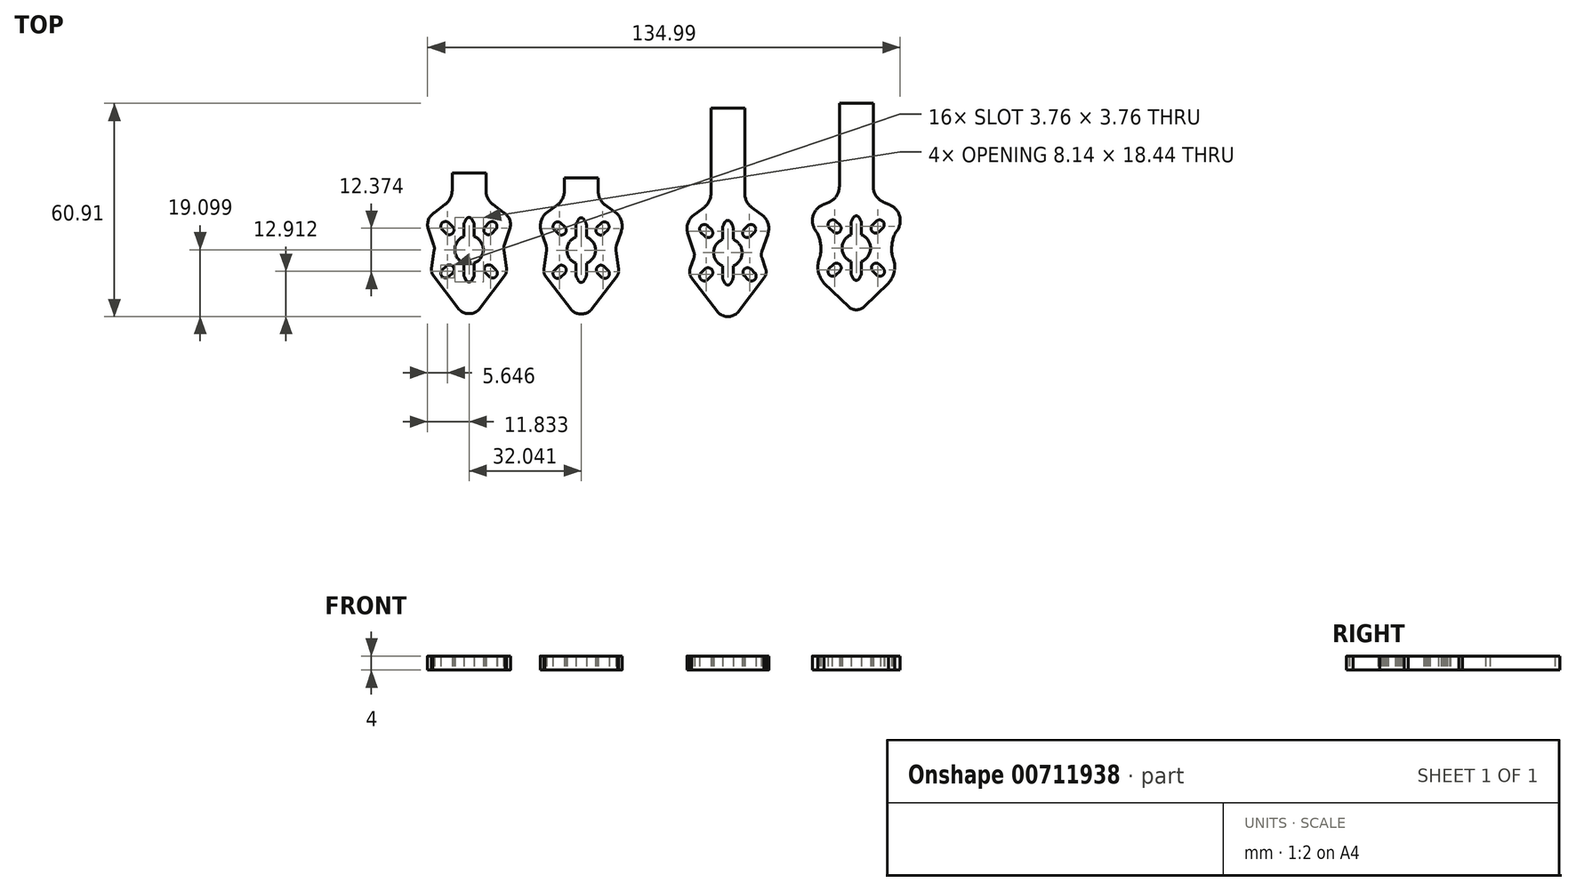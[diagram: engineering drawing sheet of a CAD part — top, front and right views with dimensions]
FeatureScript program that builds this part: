
annotation { "Feature Type Name" : "Feature", "Feature Type Description" : "" }
export const myFeature = defineFeature(function(context is Context, id is Id, definition is map)
    precondition{}
    {
        {
            var Q0;
            Q0=qCreatedBy(makeId("Top.planeOp"),FACE);
            var sketch = newSketch(context, id + "F0", { "sketchPlane" : qUnion([Q0])});
            skLineSegment(sketch, "E0", {"start": v(60.05, 27.48) * mm, "end": v(60.05, 10.08) * mm, "construction": true});
            skLineSegment(sketch, "E1", {"start": v(60.05, 27.48) * mm, "end": v(45.07, 12.5) * mm, "construction": true});
            skArc(sketch, "E2", {"start": v(53.44, 32.18) * mm, "mid": v(55.35, 32.18) * mm, "end": v(55.35, 34.1) * mm});
            skArc(sketch, "E3", {"start": v(54.29, 35.15) * mm, "mid": v(52.38, 35.15) * mm, "end": v(52.38, 33.24) * mm});
            skLineSegment(sketch, "E4", {"start": v(55.35, 34.1) * mm, "end": v(54.29, 35.15) * mm});
            skLineSegment(sketch, "E5.MirrorCS", {"start": v(53.44, 32.18) * mm, "end": v(52.38, 33.24) * mm});
            skLineSegment(sketch, "E6.MirrorCS", {"start": v(66.56, 32.18) * mm, "end": v(67.62, 33.24) * mm});
            skArc(sketch, "E7.MirrorCS", {"start": v(65.71, 35.15) * mm, "mid": v(67.62, 35.15) * mm, "end": v(67.62, 33.24) * mm});
            skLineSegment(sketch, "E8.MirrorCS", {"start": v(64.65, 34.1) * mm, "end": v(65.71, 35.15) * mm});
            skArc(sketch, "E9.MirrorCS", {"start": v(66.56, 32.18) * mm, "mid": v(64.65, 32.18) * mm, "end": v(64.65, 34.1) * mm});
            skLineSegment(sketch, "E10.MirrorCS", {"start": v(64.75, 20.87) * mm, "end": v(65.81, 19.8) * mm});
            skLineSegment(sketch, "E11.MirrorCS", {"start": v(66.66, 22.78) * mm, "end": v(67.72, 21.72) * mm});
            skArc(sketch, "E12.MirrorCS", {"start": v(66.66, 22.78) * mm, "mid": v(64.75, 22.78) * mm, "end": v(64.75, 20.87) * mm});
            skArc(sketch, "E13.MirrorCS", {"start": v(65.81, 19.8) * mm, "mid": v(67.72, 19.8) * mm, "end": v(67.72, 21.72) * mm});
            skLineSegment(sketch, "E14.MirrorCS", {"start": v(55.35, 20.87) * mm, "end": v(54.29, 19.8) * mm});
            skLineSegment(sketch, "E15.MirrorCS", {"start": v(53.44, 22.78) * mm, "end": v(52.38, 21.72) * mm});
            skArc(sketch, "E16.MirrorCS", {"start": v(54.29, 19.8) * mm, "mid": v(52.38, 19.8) * mm, "end": v(52.38, 21.72) * mm});
            skArc(sketch, "E17.MirrorCS", {"start": v(53.44, 22.78) * mm, "mid": v(55.35, 22.78) * mm, "end": v(55.35, 20.87) * mm});
            skLineSegment(sketch, "E18.left", {"start": v(61.55, 20.5) * mm, "end": v(61.55, 23.7) * mm});
            skLineSegment(sketch, "E18.right", {"start": v(58.55, 20.5) * mm, "end": v(58.55, 23.7) * mm});
            skLineSegment(sketch, "E19.trimOffspring", {"start": v(58.55, 31.27) * mm, "end": v(58.55, 34.46) * mm});
            skLineSegment(sketch, "E20.trimOffspring", {"start": v(61.55, 31.27) * mm, "end": v(61.55, 34.46) * mm});
            skArc(sketch, "E21.MirrorCS", {"start": v(69.32, 26.9) * mm, "mid": v(69.38, 26.86) * mm, "end": v(69.43, 26.82) * mm});
            skArc(sketch, "E22.MirrorCS", {"start": v(58.8, 35.43) * mm, "mid": v(58.61, 34.96) * mm, "end": v(58.55, 34.46) * mm});
            skArc(sketch, "E23.MirrorCS", {"start": v(61.55, 34.46) * mm, "mid": v(61.48, 34.96) * mm, "end": v(61.3, 35.43) * mm});
            skArc(sketch, "E24.MirrorCS", {"start": v(61.55, 20.5) * mm, "mid": v(61.48, 20) * mm, "end": v(61.3, 19.53) * mm});
            skArc(sketch, "E25.MirrorCS", {"start": v(58.8, 19.53) * mm, "mid": v(58.61, 20) * mm, "end": v(58.55, 20.5) * mm});
            skCircle(sketch, "E26", {"center": v(60.05, 27.48) * mm, "radius": 8 * mm, "construction": true});
            skLineSegment(sketch, "E27.MirrorCS", {"start": v(61.3, 35.43) * mm, "end": v(60.86, 36.22) * mm});
            skLineSegment(sketch, "E28.MirrorCS", {"start": v(58.8, 35.43) * mm, "end": v(59.24, 36.22) * mm});
            skArc(sketch, "E29.MirrorCS", {"start": v(59.24, 36.22) * mm, "mid": v(60.05, 36.7) * mm, "end": v(60.86, 36.22) * mm});
            skLineSegment(sketch, "E30.MirrorCS", {"start": v(61.95, 38.08) * mm, "end": v(58.14, 38.08) * mm});
            skPoint(sketch, "E31.visualSharp", {"position": v(68.55, 34.93) * mm});
            skPoint(sketch, "E32.MirrorCS.start.orphan", {"position": v(51.55, 36.03) * mm});
            skPoint(sketch, "E33.visualSharp", {"position": v(65.05, 10.08) * mm});
            skPoint(sketch, "E34.orphan", {"position": v(63.42, 8.64) * mm});
            skPoint(sketch, "E35", {"position": v(60.05, 38.9) * mm});
            skLineSegment(sketch, "E36.bottom", {"start": v(55.05, 68.82) * mm, "end": v(65.05, 68.82) * mm});
            skLineSegment(sketch, "E36.right", {"start": v(64.88, 70.85) * mm, "end": v(64.88, 45.12) * mm});
            skPoint(sketch, "E36.middle", {"position": v(60.05, 53.86) * mm});
            skPoint(sketch, "E37", {"position": v(60.05, 36.7) * mm});
            skPoint(sketch, "E38", {"position": v(60.05, 36.98) * mm});
            skArc(sketch, "E39", {"start": v(61.55, 23.7) * mm, "mid": v(64.12, 27.48) * mm, "end": v(61.55, 31.27) * mm});
            skArc(sketch, "E40.trimOffspring", {"start": v(58.55, 31.27) * mm, "mid": v(55.98, 27.48) * mm, "end": v(58.55, 23.7) * mm});
            skPoint(sketch, "E41.MirrorP", {"position": v(55.21, 43.47) * mm});
            skLineSegment(sketch, "E42.MirrorCS", {"start": v(55.21, 70.85) * mm, "end": v(55.21, 45.12) * mm});
            skArc(sketch, "E43.MirrorCS", {"start": v(55.21, 45.12) * mm, "mid": v(54.67, 42.86) * mm, "end": v(53.17, 41.08) * mm});
            skPoint(sketch, "E44.MirrorCS.end.orphan", {"position": v(50.72, 39.97) * mm});
            skPoint(sketch, "E45.orphan", {"position": v(68.4, 16.34) * mm});
            skPoint(sketch, "E46.orphan", {"position": v(51.7, 16.34) * mm});
            skPoint(sketch, "E47.visualSharp", {"position": v(60.05, 7.98) * mm});
            skPoint(sketch, "E48", {"position": v(48.43, 32.67) * mm});
            skArc(sketch, "E49", {"start": v(49.82, 25.54) * mm, "mid": v(49.84, 28.62) * mm, "end": v(49, 31.57) * mm});
            skArc(sketch, "E50", {"start": v(49.42, 24.36) * mm, "mid": v(49.65, 24.94) * mm, "end": v(49.82, 25.54) * mm});
            skPoint(sketch, "E51.start.orphan", {"position": v(50.18, 17.36) * mm});
            skArc(sketch, "E52", {"start": v(49.42, 24.36) * mm, "mid": v(49.23, 20.72) * mm, "end": v(50.84, 17.45) * mm});
            skArc(sketch, "E53.MirrorCS", {"start": v(70.68, 24.36) * mm, "mid": v(70.87, 20.72) * mm, "end": v(69.26, 17.45) * mm});
            skArc(sketch, "E54", {"start": v(50.72, 39.97) * mm, "mid": v(47.68, 36.65) * mm, "end": v(48.59, 32.24) * mm});
            skArc(sketch, "E55", {"start": v(50.72, 39.97) * mm, "mid": v(51.97, 40.47) * mm, "end": v(53.17, 41.08) * mm});
            skArc(sketch, "E56.filletArc", {"start": v(49, 31.57) * mm, "mid": v(48.81, 31.92) * mm, "end": v(48.59, 32.24) * mm});
            skArc(sketch, "E57.MirrorCS", {"start": v(64.88, 45.12) * mm, "mid": v(65.42, 42.86) * mm, "end": v(66.93, 41.08) * mm});
            skArc(sketch, "E58.MirrorCS", {"start": v(70.28, 25.54) * mm, "mid": v(70.26, 28.62) * mm, "end": v(71.1, 31.57) * mm});
            skArc(sketch, "E59.MirrorCS", {"start": v(70.68, 24.36) * mm, "mid": v(70.45, 24.94) * mm, "end": v(70.28, 25.54) * mm});
            skCircle(sketch, "E60", {"center": v(60.05, 27.48) * mm, "radius": 14.15 * mm, "construction": true});
            skLineSegment(sketch, "E61", {"start": v(50.84, 17.45) * mm, "end": v(57.89, 10.7) * mm});
            skLineSegment(sketch, "E62.MirrorCS", {"start": v(69.26, 17.45) * mm, "end": v(62.2, 10.7) * mm});
            skArc(sketch, "E63", {"start": v(57.89, 10.7) * mm, "mid": v(60.05, 9.84) * mm, "end": v(62.2, 10.7) * mm});
            skPoint(sketch, "E64.start.orphan", {"position": v(57.77, 9.43) * mm});
            skPoint(sketch, "E65.orphan", {"position": v(62.32, 9.43) * mm});
            skPoint(sketch, "E66.MirrorCS.end.orphan", {"position": v(69.26, 18.55) * mm});
            skPoint(sketch, "E67.MirrorCS.start.orphan", {"position": v(70.68, 24.36) * mm});
            skPoint(sketch, "E68.MirrorCS.end.orphan", {"position": v(71.5, 32.24) * mm});
            skPoint(sketch, "E69.orphan", {"position": v(71.1, 31.57) * mm});
            skArc(sketch, "E70.MirrorCS", {"start": v(69.38, 39.97) * mm, "mid": v(72.42, 36.65) * mm, "end": v(71.5, 32.24) * mm});
            skArc(sketch, "E71.MirrorCS", {"start": v(71.1, 31.57) * mm, "mid": v(71.28, 31.92) * mm, "end": v(71.5, 32.24) * mm});
            skPoint(sketch, "E72.orphan", {"position": v(66.93, 41.08) * mm});
            skPoint(sketch, "E73.MirrorCS.start.orphan", {"position": v(69.38, 39.97) * mm});
            skArc(sketch, "E74.MirrorCS", {"start": v(69.38, 39.97) * mm, "mid": v(68.13, 40.47) * mm, "end": v(66.93, 41.08) * mm});
            skLineSegment(sketch, "E75", {"start": v(60.05, 27.48) * mm, "end": v(61.4, 27.48) * mm, "construction": true});
            skLineSegment(sketch, "E76.MirrorCS", {"start": v(61.3, 19.53) * mm, "end": v(60.86, 18.74) * mm});
            skLineSegment(sketch, "E77.MirrorCS", {"start": v(58.8, 19.53) * mm, "end": v(59.24, 18.74) * mm});
            skArc(sketch, "E78.MirrorCS", {"start": v(59.24, 18.74) * mm, "mid": v(60.05, 18.26) * mm, "end": v(60.86, 18.74) * mm});
            skLineSegment(sketch, "E79", {"start": v(23.37, 26.17) * mm, "end": v(23.37, 8.78) * mm, "construction": true});
            skLineSegment(sketch, "E80", {"start": v(23.37, 26.17) * mm, "end": v(8.4, 11.2) * mm, "construction": true});
            skArc(sketch, "E81", {"start": v(16.76, 30.87) * mm, "mid": v(18.67, 30.87) * mm, "end": v(18.67, 32.78) * mm});
            skArc(sketch, "E82", {"start": v(17.6, 33.84) * mm, "mid": v(15.7, 33.84) * mm, "end": v(15.7, 31.93) * mm});
            skLineSegment(sketch, "E83", {"start": v(18.67, 32.78) * mm, "end": v(17.6, 33.84) * mm});
            skLineSegment(sketch, "E84.MirrorCS", {"start": v(16.76, 30.87) * mm, "end": v(15.7, 31.93) * mm});
            skLineSegment(sketch, "E85.MirrorCS", {"start": v(29.88, 30.87) * mm, "end": v(30.94, 31.93) * mm});
            skArc(sketch, "E86.MirrorCS", {"start": v(29.03, 33.84) * mm, "mid": v(30.94, 33.84) * mm, "end": v(30.94, 31.93) * mm});
            skLineSegment(sketch, "E87.MirrorCS", {"start": v(27.97, 32.78) * mm, "end": v(29.03, 33.84) * mm});
            skArc(sketch, "E88.MirrorCS", {"start": v(29.88, 30.87) * mm, "mid": v(27.97, 30.87) * mm, "end": v(27.97, 32.78) * mm});
            skLineSegment(sketch, "E89.MirrorCS", {"start": v(28.07, 19.56) * mm, "end": v(29.13, 18.5) * mm});
            skLineSegment(sketch, "E90.MirrorCS", {"start": v(29.98, 21.47) * mm, "end": v(31.04, 20.4) * mm});
            skArc(sketch, "E91.MirrorCS", {"start": v(29.98, 21.47) * mm, "mid": v(28.07, 21.47) * mm, "end": v(28.07, 19.56) * mm});
            skArc(sketch, "E92.MirrorCS", {"start": v(29.13, 18.5) * mm, "mid": v(31.04, 18.5) * mm, "end": v(31.04, 20.4) * mm});
            skLineSegment(sketch, "E93.MirrorCS", {"start": v(18.67, 19.56) * mm, "end": v(17.6, 18.5) * mm});
            skLineSegment(sketch, "E94.MirrorCS", {"start": v(16.76, 21.47) * mm, "end": v(15.7, 20.4) * mm});
            skArc(sketch, "E95.MirrorCS", {"start": v(17.6, 18.5) * mm, "mid": v(15.7, 18.5) * mm, "end": v(15.7, 20.4) * mm});
            skArc(sketch, "E96.MirrorCS", {"start": v(16.76, 21.47) * mm, "mid": v(18.67, 21.47) * mm, "end": v(18.67, 19.56) * mm});
            skLineSegment(sketch, "E97.left", {"start": v(24.87, 19.19) * mm, "end": v(24.87, 22.38) * mm});
            skLineSegment(sketch, "E97.right", {"start": v(21.87, 19.19) * mm, "end": v(21.87, 22.38) * mm});
            skLineSegment(sketch, "E98.trimOffspring", {"start": v(21.87, 29.96) * mm, "end": v(21.87, 33.15) * mm});
            skLineSegment(sketch, "E99.trimOffspring", {"start": v(24.87, 29.96) * mm, "end": v(24.87, 33.15) * mm});
            skArc(sketch, "E100.MirrorCS", {"start": v(22.12, 34.12) * mm, "mid": v(21.93, 33.65) * mm, "end": v(21.87, 33.15) * mm});
            skArc(sketch, "E101.MirrorCS", {"start": v(24.87, 33.15) * mm, "mid": v(24.8, 33.65) * mm, "end": v(24.62, 34.12) * mm});
            skArc(sketch, "E102.MirrorCS", {"start": v(24.87, 19.19) * mm, "mid": v(24.8, 18.69) * mm, "end": v(24.62, 18.22) * mm});
            skArc(sketch, "E103.MirrorCS", {"start": v(22.12, 18.22) * mm, "mid": v(21.93, 18.69) * mm, "end": v(21.87, 19.19) * mm});
            skCircle(sketch, "E104", {"center": v(23.37, 26.17) * mm, "radius": 8 * mm, "construction": true});
            skLineSegment(sketch, "E105.MirrorCS", {"start": v(24.62, 34.12) * mm, "end": v(24.18, 34.91) * mm});
            skLineSegment(sketch, "E106.MirrorCS", {"start": v(22.12, 34.12) * mm, "end": v(22.56, 34.91) * mm});
            skArc(sketch, "E107.MirrorCS", {"start": v(22.56, 34.91) * mm, "mid": v(23.37, 35.39) * mm, "end": v(24.18, 34.91) * mm});
            skLineSegment(sketch, "E108.MirrorCS", {"start": v(25.28, 36.77) * mm, "end": v(21.47, 36.77) * mm});
            skPoint(sketch, "E109.visualSharp", {"position": v(31.87, 33.62) * mm});
            skPoint(sketch, "E110.MirrorCS.start.orphan", {"position": v(14.87, 34.72) * mm});
            skPoint(sketch, "E111.visualSharp", {"position": v(28.37, 8.78) * mm});
            skPoint(sketch, "E112.orphan", {"position": v(26.74, 7.33) * mm});
            skPoint(sketch, "E113", {"position": v(23.37, 37.59) * mm});
            skLineSegment(sketch, "E114.bottom", {"start": v(18.37, 67.5) * mm, "end": v(28.37, 67.5) * mm});
            skLineSegment(sketch, "E114.right", {"start": v(28.2, 69.54) * mm, "end": v(28.2, 43.81) * mm});
            skPoint(sketch, "E114.middle", {"position": v(23.37, 52.55) * mm});
            skPoint(sketch, "E115", {"position": v(23.37, 35.39) * mm});
            skPoint(sketch, "E116", {"position": v(23.37, 35.67) * mm});
            skArc(sketch, "E117", {"start": v(24.87, 22.38) * mm, "mid": v(27.44, 26.17) * mm, "end": v(24.87, 29.96) * mm});
            skArc(sketch, "E118.trimOffspring", {"start": v(21.87, 29.96) * mm, "mid": v(19.3, 26.17) * mm, "end": v(21.87, 22.38) * mm});
            skPoint(sketch, "E119.MirrorP", {"position": v(18.54, 42.17) * mm});
            skLineSegment(sketch, "E120.MirrorCS", {"start": v(18.54, 69.54) * mm, "end": v(18.54, 43.81) * mm});
            skPoint(sketch, "E121.orphan", {"position": v(31.73, 15.03) * mm});
            skPoint(sketch, "E122.orphan", {"position": v(15.01, 15.03) * mm});
            skPoint(sketch, "E123.visualSharp", {"position": v(23.37, 6.68) * mm});
            skPoint(sketch, "E124.start.orphan", {"position": v(21.1, 8.12) * mm});
            skPoint(sketch, "E125.orphan", {"position": v(25.64, 8.12) * mm});
            skPoint(sketch, "E126.MirrorCS.end.orphan", {"position": v(32.58, 17.24) * mm});
            skPoint(sketch, "E127.MirrorCS.start.orphan", {"position": v(34, 23.05) * mm});
            skPoint(sketch, "E128.MirrorCS.end.orphan", {"position": v(34.83, 30.93) * mm});
            skPoint(sketch, "E129.orphan", {"position": v(34.42, 30.26) * mm});
            skPoint(sketch, "E130.orphan", {"position": v(30.25, 39.78) * mm});
            skPoint(sketch, "E131.MirrorCS.start.orphan", {"position": v(32.7, 38.66) * mm});
            skLineSegment(sketch, "E132", {"start": v(23.37, 26.17) * mm, "end": v(24.73, 26.17) * mm, "construction": true});
            skLineSegment(sketch, "E133.MirrorCS", {"start": v(24.62, 18.22) * mm, "end": v(24.18, 17.43) * mm});
            skLineSegment(sketch, "E134.MirrorCS", {"start": v(22.12, 18.22) * mm, "end": v(22.56, 17.43) * mm});
            skArc(sketch, "E135.MirrorCS", {"start": v(22.56, 17.43) * mm, "mid": v(23.37, 16.95) * mm, "end": v(24.18, 17.43) * mm});
            skLineSegment(sketch, "E136", {"start": v(33.1, 26.52) * mm, "end": v(34.77, 31.43) * mm});
            skPoint(sketch, "E137.visualSharp", {"position": v(35.8, 34.45) * mm});
            skArc(sketch, "E137.filletArc", {"start": v(34.77, 31.43) * mm, "mid": v(34.9, 34.23) * mm, "end": v(33.5, 36.66) * mm});
            skLineSegment(sketch, "E138", {"start": v(34.11, 21.79) * mm, "end": v(33.12, 24.52) * mm});
            skPoint(sketch, "E139.visualSharp", {"position": v(34.65, 20.3) * mm});
            skArc(sketch, "E139.filletArc", {"start": v(33.75, 19.02) * mm, "mid": v(34.27, 20.36) * mm, "end": v(34.11, 21.79) * mm});
            skPoint(sketch, "E140.visualSharp", {"position": v(32.75, 25.51) * mm});
            skArc(sketch, "E140.filletArc", {"start": v(33.1, 26.52) * mm, "mid": v(32.93, 25.51) * mm, "end": v(33.12, 24.52) * mm});
            skPoint(sketch, "E141.MirrorP", {"position": v(10.94, 34.45) * mm});
            skLineSegment(sketch, "E142.MirrorCS", {"start": v(13, 19.02) * mm, "end": v(14.4, 17.2) * mm});
            skPoint(sketch, "E143.MirrorP", {"position": v(14.16, 17.24) * mm});
            skLineSegment(sketch, "E144.MirrorCS", {"start": v(12.63, 21.79) * mm, "end": v(13.63, 24.52) * mm});
            skArc(sketch, "E145.MirrorCS", {"start": v(13, 19.02) * mm, "mid": v(12.47, 20.36) * mm, "end": v(12.63, 21.79) * mm});
            skPoint(sketch, "E146.MirrorP", {"position": v(11.91, 30.93) * mm});
            skPoint(sketch, "E147.MirrorP", {"position": v(14.04, 38.66) * mm});
            skPoint(sketch, "E148.MirrorP", {"position": v(14.87, 33.62) * mm});
            skPoint(sketch, "E149.MirrorP", {"position": v(12.09, 20.3) * mm});
            skPoint(sketch, "E150.MirrorP", {"position": v(12.32, 30.26) * mm});
            skArc(sketch, "E151.MirrorCS", {"start": v(11.97, 31.43) * mm, "mid": v(11.84, 34.23) * mm, "end": v(13.24, 36.66) * mm});
            skPoint(sketch, "E152.MirrorP", {"position": v(12.74, 23.05) * mm});
            skLineSegment(sketch, "E153", {"start": v(18.54, 43.81) * mm, "end": v(18.54, 43.07) * mm});
            skPoint(sketch, "E154.end.orphan", {"position": v(17.09, 39.24) * mm});
            skPoint(sketch, "E155.MirrorCS.end.orphan", {"position": v(29.65, 39.24) * mm});
            skPoint(sketch, "E155.MirrorCS.start.orphan", {"position": v(33.5, 36.66) * mm});
            skLineSegment(sketch, "E156", {"start": v(13.24, 36.66) * mm, "end": v(16.49, 39.04) * mm});
            skPoint(sketch, "E157.visualSharp", {"position": v(18.54, 40.54) * mm});
            skArc(sketch, "E157.filletArc", {"start": v(16.49, 39.04) * mm, "mid": v(18, 40.81) * mm, "end": v(18.54, 43.07) * mm});
            skPoint(sketch, "E158.MirrorCS.end.orphan", {"position": v(16.49, 39.78) * mm});
            skPoint(sketch, "E159.MirrorCS.start.orphan", {"position": v(28.2, 43.81) * mm});
            skPoint(sketch, "E160.MirrorCS.end.orphan", {"position": v(28.2, 40.54) * mm});
            skArc(sketch, "E161.MirrorCS", {"start": v(30.25, 39.04) * mm, "mid": v(28.75, 40.81) * mm, "end": v(28.2, 43.07) * mm});
            skLineSegment(sketch, "E162.MirrorCS", {"start": v(33.5, 36.66) * mm, "end": v(30.25, 39.04) * mm});
            skLineSegment(sketch, "E163.MirrorCS", {"start": v(28.2, 43.81) * mm, "end": v(28.2, 43.07) * mm});
            skCircle(sketch, "E164", {"center": v(23.37, 26.17) * mm, "radius": 14.15 * mm, "construction": true});
            skLineSegment(sketch, "E165", {"start": v(14.4, 17.2) * mm, "end": v(20.56, 9.1) * mm});
            skLineSegment(sketch, "E166.MirrorCS", {"start": v(33.75, 19.02) * mm, "end": v(26.18, 9.1) * mm});
            skArc(sketch, "E167", {"start": v(20.95, 8.71) * mm, "mid": v(23.37, 7.91) * mm, "end": v(25.79, 8.71) * mm});
            skPoint(sketch, "E168.orphan", {"position": v(20.83, 8.74) * mm});
            skPoint(sketch, "E169.orphan", {"position": v(25.9, 8.74) * mm});
            skPoint(sketch, "E170.visualSharp", {"position": v(20.7, 8.92) * mm});
            skArc(sketch, "E170.filletArc", {"start": v(20.56, 9.1) * mm, "mid": v(20.74, 8.9) * mm, "end": v(20.95, 8.71) * mm});
            skPoint(sketch, "E171.visualSharp", {"position": v(26.04, 8.92) * mm});
            skArc(sketch, "E171.filletArc", {"start": v(25.79, 8.71) * mm, "mid": v(26, 8.9) * mm, "end": v(26.18, 9.1) * mm});
            skLineSegment(sketch, "E172", {"start": v(-18.53, 26.9) * mm, "end": v(-18.53, 9.5) * mm, "construction": true});
            skLineSegment(sketch, "E173", {"start": v(-18.53, 26.9) * mm, "end": v(-33.5, 11.93) * mm, "construction": true});
            skArc(sketch, "E174", {"start": v(-25.14, 31.6) * mm, "mid": v(-23.23, 31.6) * mm, "end": v(-23.23, 33.51) * mm});
            skArc(sketch, "E175", {"start": v(-24.29, 34.57) * mm, "mid": v(-26.2, 34.57) * mm, "end": v(-26.2, 32.67) * mm});
            skLineSegment(sketch, "E176", {"start": v(-23.23, 33.51) * mm, "end": v(-24.29, 34.57) * mm});
            skLineSegment(sketch, "E177.MirrorCS", {"start": v(-25.14, 31.6) * mm, "end": v(-26.2, 32.67) * mm});
            skLineSegment(sketch, "E178.MirrorCS", {"start": v(-12.02, 31.6) * mm, "end": v(-10.95, 32.67) * mm});
            skArc(sketch, "E179.MirrorCS", {"start": v(-12.86, 34.57) * mm, "mid": v(-10.95, 34.57) * mm, "end": v(-10.95, 32.67) * mm});
            skLineSegment(sketch, "E180.MirrorCS", {"start": v(-13.92, 33.51) * mm, "end": v(-12.86, 34.57) * mm});
            skArc(sketch, "E181.MirrorCS", {"start": v(-12.02, 31.6) * mm, "mid": v(-13.92, 31.6) * mm, "end": v(-13.92, 33.51) * mm});
            skLineSegment(sketch, "E182.MirrorCS", {"start": v(-13.82, 20.3) * mm, "end": v(-12.76, 19.23) * mm});
            skLineSegment(sketch, "E183.MirrorCS", {"start": v(-11.91, 22.2) * mm, "end": v(-10.85, 21.14) * mm});
            skArc(sketch, "E184.MirrorCS", {"start": v(-11.91, 22.2) * mm, "mid": v(-13.82, 22.2) * mm, "end": v(-13.82, 20.3) * mm});
            skArc(sketch, "E185.MirrorCS", {"start": v(-12.76, 19.23) * mm, "mid": v(-10.85, 19.23) * mm, "end": v(-10.85, 21.14) * mm});
            skLineSegment(sketch, "E186.MirrorCS", {"start": v(-23.23, 20.3) * mm, "end": v(-24.29, 19.23) * mm});
            skLineSegment(sketch, "E187.MirrorCS", {"start": v(-25.14, 22.2) * mm, "end": v(-26.2, 21.14) * mm});
            skArc(sketch, "E188.MirrorCS", {"start": v(-24.29, 19.23) * mm, "mid": v(-26.2, 19.23) * mm, "end": v(-26.2, 21.14) * mm});
            skArc(sketch, "E189.MirrorCS", {"start": v(-25.14, 22.2) * mm, "mid": v(-23.23, 22.2) * mm, "end": v(-23.23, 20.3) * mm});
            skLineSegment(sketch, "E190.left", {"start": v(-17.03, 19.92) * mm, "end": v(-17.03, 23.12) * mm});
            skLineSegment(sketch, "E190.right", {"start": v(-20.03, 19.92) * mm, "end": v(-20.03, 23.12) * mm});
            skLineSegment(sketch, "E191.trimOffspring", {"start": v(-20.03, 30.69) * mm, "end": v(-20.03, 33.89) * mm});
            skLineSegment(sketch, "E192.trimOffspring", {"start": v(-17.03, 30.69) * mm, "end": v(-17.03, 33.89) * mm});
            skArc(sketch, "E193.MirrorCS", {"start": v(-19.77, 34.86) * mm, "mid": v(-19.96, 34.39) * mm, "end": v(-20.03, 33.89) * mm});
            skArc(sketch, "E194.MirrorCS", {"start": v(-17.03, 33.89) * mm, "mid": v(-17.09, 34.39) * mm, "end": v(-17.28, 34.86) * mm});
            skArc(sketch, "E195.MirrorCS", {"start": v(-17.03, 19.92) * mm, "mid": v(-17.09, 19.42) * mm, "end": v(-17.28, 18.95) * mm});
            skArc(sketch, "E196.MirrorCS", {"start": v(-19.77, 18.95) * mm, "mid": v(-19.96, 19.42) * mm, "end": v(-20.03, 19.92) * mm});
            skCircle(sketch, "E197", {"center": v(-18.53, 26.9) * mm, "radius": 8 * mm, "construction": true});
            skLineSegment(sketch, "E198.MirrorCS", {"start": v(-17.28, 34.86) * mm, "end": v(-17.71, 35.64) * mm});
            skLineSegment(sketch, "E199.MirrorCS", {"start": v(-19.77, 34.86) * mm, "end": v(-19.34, 35.64) * mm});
            skArc(sketch, "E200.MirrorCS", {"start": v(-19.34, 35.64) * mm, "mid": v(-18.53, 36.12) * mm, "end": v(-17.71, 35.64) * mm});
            skPoint(sketch, "E201.visualSharp", {"position": v(-13.53, 9.5) * mm});
            skPoint(sketch, "E202", {"position": v(-18.53, 36.4) * mm});
            skArc(sketch, "E203", {"start": v(-17.03, 23.12) * mm, "mid": v(-14.45, 26.9) * mm, "end": v(-17.03, 30.69) * mm});
            skArc(sketch, "E204.trimOffspring", {"start": v(-20.03, 30.69) * mm, "mid": v(-22.6, 26.9) * mm, "end": v(-20.03, 23.12) * mm});
            skPoint(sketch, "E205.MirrorP", {"position": v(-18.53, 38.32) * mm});
            skPoint(sketch, "E206.MirrorCS.end.orphan", {"position": v(-7.07, 31.67) * mm});
            skPoint(sketch, "E207.orphan", {"position": v(-7.48, 31) * mm});
            skLineSegment(sketch, "E208", {"start": v(-18.53, 26.9) * mm, "end": v(-17.17, 26.9) * mm, "construction": true});
            skLineSegment(sketch, "E209.MirrorCS", {"start": v(-17.28, 18.95) * mm, "end": v(-17.71, 18.16) * mm});
            skLineSegment(sketch, "E210.MirrorCS", {"start": v(-19.77, 18.95) * mm, "end": v(-19.34, 18.16) * mm});
            skArc(sketch, "E211.MirrorCS", {"start": v(-19.34, 18.16) * mm, "mid": v(-18.53, 17.68) * mm, "end": v(-17.71, 18.16) * mm});
            skLineSegment(sketch, "E212", {"start": v(-8.46, 28.25) * mm, "end": v(-7.12, 32.16) * mm});
            skPoint(sketch, "E213.MirrorCS.end.orphan", {"position": v(-11.64, 40.5) * mm});
            skArc(sketch, "E214.filletArc", {"start": v(-7.12, 32.16) * mm, "mid": v(-7, 34.96) * mm, "end": v(-8.4, 37.39) * mm});
            skLineSegment(sketch, "E215", {"start": v(-7.85, 21.55) * mm, "end": v(-8.6, 26.87) * mm});
            skArc(sketch, "E216.filletArc", {"start": v(-8.15, 19.76) * mm, "mid": v(-7.86, 20.63) * mm, "end": v(-7.85, 21.55) * mm});
            skArc(sketch, "E217.filletArc", {"start": v(-8.46, 28.25) * mm, "mid": v(-8.6, 27.57) * mm, "end": v(-8.6, 26.87) * mm});
            skLineSegment(sketch, "E218.MirrorCS", {"start": v(-28.9, 19.76) * mm, "end": v(-27.5, 17.92) * mm});
            skLineSegment(sketch, "E219.MirrorCS", {"start": v(-29.2, 21.55) * mm, "end": v(-28.46, 26.87) * mm});
            skArc(sketch, "E220.MirrorCS", {"start": v(-28.9, 19.76) * mm, "mid": v(-29.2, 20.63) * mm, "end": v(-29.2, 21.55) * mm});
            skPoint(sketch, "E221.MirrorP", {"position": v(-27.86, 39.4) * mm});
            skArc(sketch, "E222.MirrorCS", {"start": v(-29.93, 32.16) * mm, "mid": v(-30.06, 34.96) * mm, "end": v(-28.66, 37.39) * mm});
            skPoint(sketch, "E223.MirrorP", {"position": v(-29.99, 31.67) * mm});
            skLineSegment(sketch, "E224", {"start": v(-23.36, 44.54) * mm, "end": v(-23.36, 43.8) * mm});
            skPoint(sketch, "E225.end.orphan", {"position": v(-24.8, 39.97) * mm});
            skPoint(sketch, "E226.MirrorCS.end.orphan", {"position": v(-12.25, 39.97) * mm});
            skPoint(sketch, "E226.MirrorCS.start.orphan", {"position": v(-8.4, 37.39) * mm});
            skLineSegment(sketch, "E227", {"start": v(-28.66, 37.39) * mm, "end": v(-25.4, 39.77) * mm});
            skArc(sketch, "E228.filletArc", {"start": v(-25.4, 39.77) * mm, "mid": v(-23.9, 41.54) * mm, "end": v(-23.36, 43.8) * mm});
            skPoint(sketch, "E229.MirrorCS.end.orphan", {"position": v(-13.7, 41.27) * mm});
            skArc(sketch, "E230.MirrorCS", {"start": v(-11.65, 39.77) * mm, "mid": v(-13.15, 41.54) * mm, "end": v(-13.7, 43.8) * mm});
            skLineSegment(sketch, "E231.MirrorCS", {"start": v(-8.4, 37.39) * mm, "end": v(-11.65, 39.77) * mm});
            skLineSegment(sketch, "E232.MirrorCS", {"start": v(-13.7, 44.54) * mm, "end": v(-13.7, 43.8) * mm});
            skCircle(sketch, "E233", {"center": v(-18.53, 26.9) * mm, "radius": 14.15 * mm, "construction": true});
            skLineSegment(sketch, "E234", {"start": v(-27.5, 17.92) * mm, "end": v(-21.34, 9.84) * mm});
            skLineSegment(sketch, "E235.MirrorCS", {"start": v(-8.15, 19.76) * mm, "end": v(-15.71, 9.84) * mm});
            skArc(sketch, "E236", {"start": v(-20.94, 9.45) * mm, "mid": v(-18.53, 8.65) * mm, "end": v(-16.11, 9.45) * mm});
            skPoint(sketch, "E237.start.orphan", {"position": v(-21.06, 9.48) * mm});
            skPoint(sketch, "E238.orphan", {"position": v(-15.99, 9.48) * mm});
            skArc(sketch, "E239.filletArc", {"start": v(-21.34, 9.84) * mm, "mid": v(-21.15, 9.63) * mm, "end": v(-20.94, 9.45) * mm});
            skArc(sketch, "E240.filletArc", {"start": v(-16.11, 9.45) * mm, "mid": v(-15.9, 9.63) * mm, "end": v(-15.71, 9.84) * mm});
            skLineSegment(sketch, "E241.MirrorCS", {"start": v(-28.6, 28.25) * mm, "end": v(-29.93, 32.16) * mm});
            skArc(sketch, "E242.MirrorCS", {"start": v(-28.6, 28.25) * mm, "mid": v(-28.45, 27.57) * mm, "end": v(-28.46, 26.87) * mm});
            skLineSegment(sketch, "E243.MirrorCS", {"start": v(13.65, 26.52) * mm, "end": v(11.97, 31.43) * mm});
            skArc(sketch, "E244.MirrorCS", {"start": v(13.65, 26.52) * mm, "mid": v(13.8, 25.51) * mm, "end": v(13.63, 24.52) * mm});
            skLineSegment(sketch, "E245", {"start": v(-50.57, 27) * mm, "end": v(-50.57, 9.61) * mm, "construction": true});
            skLineSegment(sketch, "E246", {"start": v(-50.57, 27) * mm, "end": v(-65.54, 12.03) * mm, "construction": true});
            skArc(sketch, "E247", {"start": v(-57.18, 31.71) * mm, "mid": v(-55.27, 31.71) * mm, "end": v(-55.27, 33.62) * mm});
            skArc(sketch, "E248", {"start": v(-56.33, 34.68) * mm, "mid": v(-58.24, 34.68) * mm, "end": v(-58.24, 32.77) * mm});
            skLineSegment(sketch, "E249", {"start": v(-55.27, 33.62) * mm, "end": v(-56.33, 34.68) * mm});
            skLineSegment(sketch, "E250.MirrorCS", {"start": v(-57.18, 31.71) * mm, "end": v(-58.24, 32.77) * mm});
            skLineSegment(sketch, "E251.MirrorCS", {"start": v(-44.06, 31.71) * mm, "end": v(-43, 32.77) * mm});
            skArc(sketch, "E252.MirrorCS", {"start": v(-44.9, 34.68) * mm, "mid": v(-43, 34.68) * mm, "end": v(-43, 32.77) * mm});
            skLineSegment(sketch, "E253.MirrorCS", {"start": v(-45.97, 33.62) * mm, "end": v(-44.9, 34.68) * mm});
            skArc(sketch, "E254.MirrorCS", {"start": v(-44.06, 31.71) * mm, "mid": v(-45.97, 31.71) * mm, "end": v(-45.97, 33.62) * mm});
            skLineSegment(sketch, "E255.MirrorCS", {"start": v(-45.86, 20.4) * mm, "end": v(-44.8, 19.34) * mm});
            skLineSegment(sketch, "E256.MirrorCS", {"start": v(-43.96, 22.3) * mm, "end": v(-42.9, 21.25) * mm});
            skArc(sketch, "E257.MirrorCS", {"start": v(-43.96, 22.3) * mm, "mid": v(-45.86, 22.3) * mm, "end": v(-45.86, 20.4) * mm});
            skArc(sketch, "E258.MirrorCS", {"start": v(-44.8, 19.34) * mm, "mid": v(-42.9, 19.34) * mm, "end": v(-42.9, 21.25) * mm});
            skLineSegment(sketch, "E259.MirrorCS", {"start": v(-55.27, 20.4) * mm, "end": v(-56.33, 19.34) * mm});
            skLineSegment(sketch, "E260.MirrorCS", {"start": v(-57.18, 22.3) * mm, "end": v(-58.24, 21.25) * mm});
            skArc(sketch, "E261.MirrorCS", {"start": v(-56.33, 19.34) * mm, "mid": v(-58.24, 19.34) * mm, "end": v(-58.24, 21.25) * mm});
            skArc(sketch, "E262.MirrorCS", {"start": v(-57.18, 22.3) * mm, "mid": v(-55.27, 22.3) * mm, "end": v(-55.27, 20.4) * mm});
            skLineSegment(sketch, "E263.left", {"start": v(-49.07, 20.03) * mm, "end": v(-49.07, 23.22) * mm});
            skLineSegment(sketch, "E263.right", {"start": v(-52.07, 20.03) * mm, "end": v(-52.07, 23.22) * mm});
            skLineSegment(sketch, "E264.trimOffspring", {"start": v(-52.07, 30.8) * mm, "end": v(-52.07, 34) * mm});
            skLineSegment(sketch, "E265.trimOffspring", {"start": v(-49.07, 30.8) * mm, "end": v(-49.07, 34) * mm});
            skArc(sketch, "E266.MirrorCS", {"start": v(-51.82, 34.96) * mm, "mid": v(-52, 34.5) * mm, "end": v(-52.07, 34) * mm});
            skArc(sketch, "E267.MirrorCS", {"start": v(-49.07, 34) * mm, "mid": v(-49.13, 34.5) * mm, "end": v(-49.32, 34.96) * mm});
            skArc(sketch, "E268.MirrorCS", {"start": v(-49.07, 20.03) * mm, "mid": v(-49.13, 19.53) * mm, "end": v(-49.32, 19.06) * mm});
            skArc(sketch, "E269.MirrorCS", {"start": v(-51.82, 19.06) * mm, "mid": v(-52, 19.53) * mm, "end": v(-52.07, 20.03) * mm});
            skCircle(sketch, "E270", {"center": v(-50.57, 27) * mm, "radius": 8 * mm, "construction": true});
            skLineSegment(sketch, "E271.MirrorCS", {"start": v(-49.32, 34.96) * mm, "end": v(-49.75, 35.75) * mm});
            skLineSegment(sketch, "E272.MirrorCS", {"start": v(-51.82, 34.96) * mm, "end": v(-51.38, 35.75) * mm});
            skArc(sketch, "E273.MirrorCS", {"start": v(-51.38, 35.75) * mm, "mid": v(-50.57, 36.23) * mm, "end": v(-49.75, 35.75) * mm});
            skPoint(sketch, "E274.visualSharp", {"position": v(-42.07, 34.46) * mm});
            skPoint(sketch, "E275.MirrorCS.start.orphan", {"position": v(-59.07, 35.56) * mm});
            skPoint(sketch, "E276.visualSharp", {"position": v(-45.57, 9.61) * mm});
            skPoint(sketch, "E277.orphan", {"position": v(-47.2, 8.17) * mm});
            skPoint(sketch, "E278", {"position": v(-50.57, 38.43) * mm});
            skPoint(sketch, "E279", {"position": v(-50.57, 36.23) * mm});
            skPoint(sketch, "E280", {"position": v(-50.57, 36.5) * mm});
            skArc(sketch, "E281", {"start": v(-49.07, 23.22) * mm, "mid": v(-46.5, 27) * mm, "end": v(-49.07, 30.8) * mm});
            skArc(sketch, "E282.trimOffspring", {"start": v(-52.07, 30.8) * mm, "mid": v(-54.64, 27) * mm, "end": v(-52.07, 23.22) * mm});
            skPoint(sketch, "E283.MirrorP", {"position": v(-55.4, 43) * mm});
            skPoint(sketch, "E284.orphan", {"position": v(-42.2, 15.87) * mm});
            skPoint(sketch, "E285.orphan", {"position": v(-58.92, 15.87) * mm});
            skPoint(sketch, "E286.visualSharp", {"position": v(-50.57, 7.51) * mm});
            skPoint(sketch, "E287.start.orphan", {"position": v(-52.84, 8.96) * mm});
            skPoint(sketch, "E288.orphan", {"position": v(-48.3, 8.96) * mm});
            skPoint(sketch, "E289.MirrorCS.end.orphan", {"position": v(-41.36, 18.08) * mm});
            skPoint(sketch, "E290.MirrorCS.start.orphan", {"position": v(-39.94, 23.9) * mm});
            skPoint(sketch, "E291.MirrorCS.end.orphan", {"position": v(-39.1, 31.77) * mm});
            skPoint(sketch, "E292.orphan", {"position": v(-39.52, 31.1) * mm});
            skPoint(sketch, "E293.orphan", {"position": v(-43.68, 40.61) * mm});
            skPoint(sketch, "E294.MirrorCS.start.orphan", {"position": v(-41.24, 39.5) * mm});
            skLineSegment(sketch, "E295", {"start": v(-50.57, 27) * mm, "end": v(-49.2, 27) * mm, "construction": true});
            skLineSegment(sketch, "E296.MirrorCS", {"start": v(-49.32, 19.06) * mm, "end": v(-49.75, 18.27) * mm});
            skLineSegment(sketch, "E297.MirrorCS", {"start": v(-51.82, 19.06) * mm, "end": v(-51.38, 18.27) * mm});
            skArc(sketch, "E298.MirrorCS", {"start": v(-51.38, 18.27) * mm, "mid": v(-50.57, 17.8) * mm, "end": v(-49.75, 18.27) * mm});
            skLineSegment(sketch, "E299", {"start": v(-40.5, 28.36) * mm, "end": v(-39.16, 32.27) * mm});
            skPoint(sketch, "E300.visualSharp", {"position": v(-38.13, 35.29) * mm});
            skLineSegment(sketch, "E301", {"start": v(-39.89, 21.65) * mm, "end": v(-40.63, 26.98) * mm});
            skPoint(sketch, "E302.visualSharp", {"position": v(-39.88, 21.57) * mm});
            skArc(sketch, "E302.filletArc", {"start": v(-40.2, 19.86) * mm, "mid": v(-39.9, 20.73) * mm, "end": v(-39.89, 21.65) * mm});
            skPoint(sketch, "E303.visualSharp", {"position": v(-40.73, 27.68) * mm});
            skArc(sketch, "E303.filletArc", {"start": v(-40.5, 28.36) * mm, "mid": v(-40.65, 27.68) * mm, "end": v(-40.63, 26.98) * mm});
            skPoint(sketch, "E304.MirrorP", {"position": v(-63, 35.29) * mm});
            skLineSegment(sketch, "E305.MirrorCS", {"start": v(-60.94, 19.86) * mm, "end": v(-59.55, 18.03) * mm});
            skPoint(sketch, "E306.MirrorP", {"position": v(-59.77, 18.08) * mm});
            skLineSegment(sketch, "E307.MirrorCS", {"start": v(-61.25, 21.65) * mm, "end": v(-60.5, 26.98) * mm});
            skArc(sketch, "E308.MirrorCS", {"start": v(-60.94, 19.86) * mm, "mid": v(-61.23, 20.73) * mm, "end": v(-61.25, 21.65) * mm});
            skPoint(sketch, "E309.MirrorP", {"position": v(-62.03, 31.77) * mm});
            skPoint(sketch, "E310.MirrorP", {"position": v(-59.9, 39.5) * mm});
            skPoint(sketch, "E311.MirrorP", {"position": v(-59.07, 34.46) * mm});
            skPoint(sketch, "E312.MirrorP", {"position": v(-61.26, 21.57) * mm});
            skPoint(sketch, "E313.MirrorP", {"position": v(-61.62, 31.1) * mm});
            skPoint(sketch, "E314.MirrorP", {"position": v(-61.2, 23.9) * mm});
            skLineSegment(sketch, "E315", {"start": v(-55.4, 44.65) * mm, "end": v(-55.4, 43.91) * mm});
            skPoint(sketch, "E316.end.orphan", {"position": v(-56.85, 40.08) * mm});
            skPoint(sketch, "E317.MirrorCS.end.orphan", {"position": v(-44.29, 40.08) * mm});
            skPoint(sketch, "E317.MirrorCS.start.orphan", {"position": v(-40.43, 37.5) * mm});
            skPoint(sketch, "E318.visualSharp", {"position": v(-55.4, 41.38) * mm});
            skArc(sketch, "E318.filletArc", {"start": v(-57.45, 39.88) * mm, "mid": v(-55.94, 41.65) * mm, "end": v(-55.4, 43.91) * mm});
            skPoint(sketch, "E319.MirrorCS.end.orphan", {"position": v(-57.45, 40.61) * mm});
            skPoint(sketch, "E320.MirrorCS.end.orphan", {"position": v(-45.73, 41.38) * mm});
            skArc(sketch, "E321.MirrorCS", {"start": v(-43.69, 39.88) * mm, "mid": v(-45.2, 41.65) * mm, "end": v(-45.73, 43.91) * mm});
            skLineSegment(sketch, "E322.MirrorCS", {"start": v(-45.73, 44.65) * mm, "end": v(-45.73, 43.91) * mm});
            skCircle(sketch, "E323", {"center": v(-50.57, 27) * mm, "radius": 14.15 * mm, "construction": true});
            skLineSegment(sketch, "E324", {"start": v(-59.55, 18.03) * mm, "end": v(-53.38, 9.94) * mm});
            skLineSegment(sketch, "E325.MirrorCS", {"start": v(-40.2, 19.86) * mm, "end": v(-47.75, 9.94) * mm});
            skArc(sketch, "E326", {"start": v(-52.98, 9.55) * mm, "mid": v(-50.57, 8.75) * mm, "end": v(-48.15, 9.55) * mm});
            skPoint(sketch, "E327.orphan", {"position": v(-53.1, 9.58) * mm});
            skPoint(sketch, "E328.orphan", {"position": v(-48.03, 9.58) * mm});
            skLineSegment(sketch, "E329.bottom", {"start": v(-55.84, 8.76) * mm, "end": v(-62.42, 8.76) * mm});
            skPoint(sketch, "E330.visualSharp", {"position": v(-53.24, 9.76) * mm});
            skArc(sketch, "E330.filletArc", {"start": v(-53.38, 9.94) * mm, "mid": v(-53.2, 9.73) * mm, "end": v(-52.98, 9.55) * mm});
            skPoint(sketch, "E331.visualSharp", {"position": v(-47.9, 9.76) * mm});
            skArc(sketch, "E331.filletArc", {"start": v(-48.15, 9.55) * mm, "mid": v(-47.94, 9.73) * mm, "end": v(-47.75, 9.94) * mm});
            skArc(sketch, "E332.MirrorCS", {"start": v(-60.63, 28.36) * mm, "mid": v(-60.49, 27.68) * mm, "end": v(-60.5, 26.98) * mm});
            skLineSegment(sketch, "E333", {"start": v(-60.63, 28.36) * mm, "end": v(-61.97, 32.27) * mm});
            skLineSegment(sketch, "E334", {"start": v(-61.97, 32.27) * mm, "end": v(-62.19, 32.9) * mm});
            skPoint(sketch, "E335.visualSharp", {"position": v(-63.25, 36.02) * mm});
            skArc(sketch, "E335.filletArc", {"start": v(-60.4, 37.67) * mm, "mid": v(-62.15, 35.6) * mm, "end": v(-62.19, 32.9) * mm});
            skLineSegment(sketch, "E336", {"start": v(-60.4, 37.67) * mm, "end": v(-57.45, 39.88) * mm});
            skLineSegment(sketch, "E337.MirrorCS", {"start": v(-39.16, 32.27) * mm, "end": v(-38.95, 32.9) * mm});
            skArc(sketch, "E338.MirrorCS", {"start": v(-40.73, 37.67) * mm, "mid": v(-38.98, 35.6) * mm, "end": v(-38.95, 32.9) * mm});
            skLineSegment(sketch, "E339.MirrorCS", {"start": v(-40.73, 37.67) * mm, "end": v(-43.69, 39.88) * mm});
            skLineSegment(sketch, "E340", {"start": v(-55.4, 44.65) * mm, "end": v(-55.4, 48.9) * mm});
            skLineSegment(sketch, "E341.MirrorCS", {"start": v(-45.73, 44.65) * mm, "end": v(-45.73, 48.9) * mm});
            skLineSegment(sketch, "E342", {"start": v(-55.4, 48.9) * mm, "end": v(-45.73, 48.9) * mm});
            skLineSegment(sketch, "E343", {"start": v(-23.36, 44.54) * mm, "end": v(-23.36, 47.58) * mm});
            skLineSegment(sketch, "E344.MirrorCS", {"start": v(-13.7, 44.54) * mm, "end": v(-13.7, 47.58) * mm});
            skLineSegment(sketch, "E345", {"start": v(-13.7, 47.58) * mm, "end": v(-23.36, 47.58) * mm});
            skSolve(sketch);
        }
        {
            var Q0;
            Q0 = qSketchRegion(id + "F0", true);
            extrude(context, id + "F1", {"entities" : qUnion([Q0]), "depth" : 4 * mm, "offsetDistance" : 25 * mm});
        }
    });
